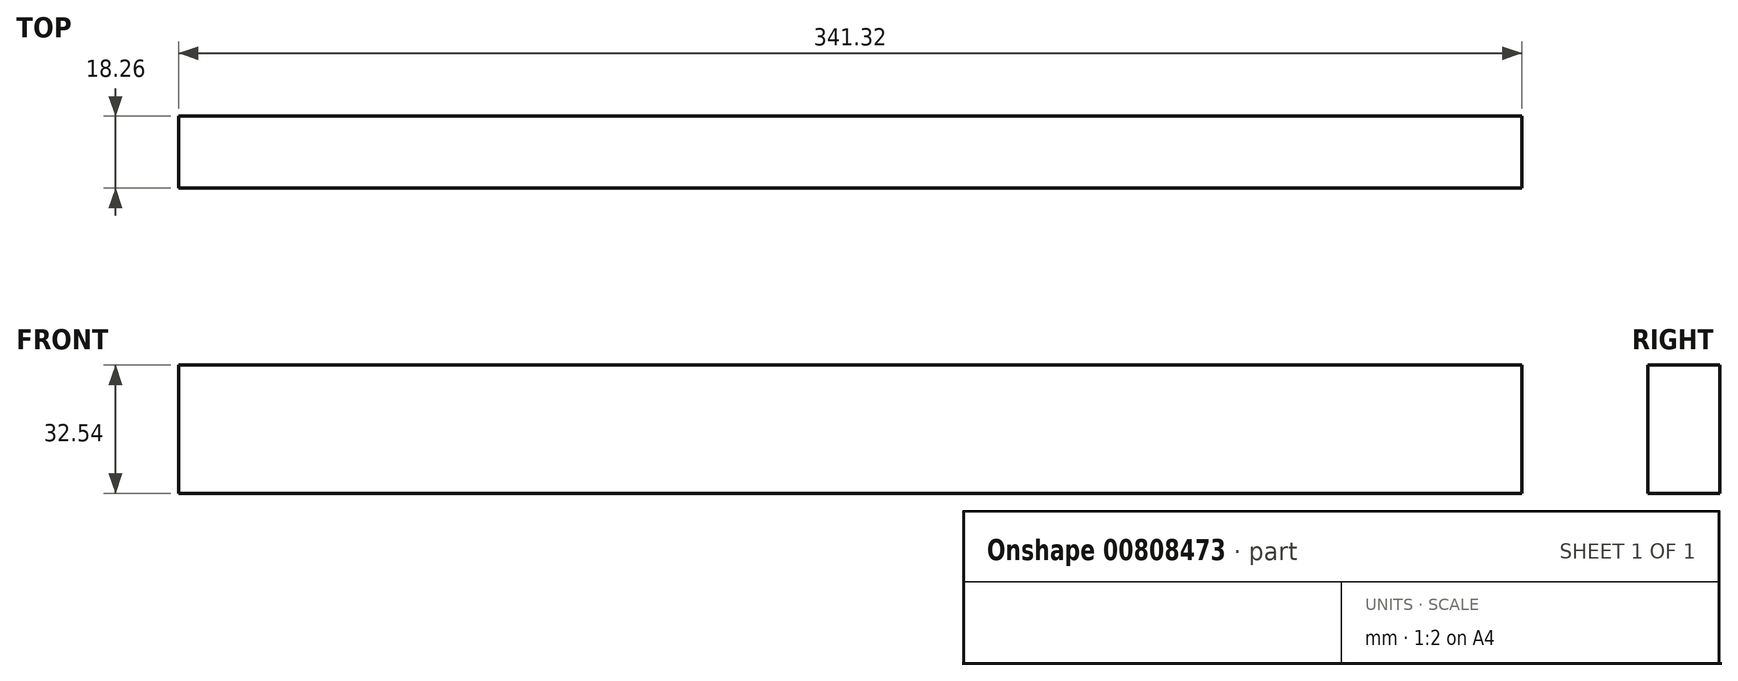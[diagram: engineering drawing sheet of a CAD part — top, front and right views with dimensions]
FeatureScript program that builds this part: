
annotation { "Feature Type Name" : "Feature", "Feature Type Description" : "" }
export const myFeature = defineFeature(function(context is Context, id is Id, definition is map)
    precondition{}
    {
        {
            var Q0;
            Q0=qCreatedBy(makeId("Front.planeOp"),FACE);
            var sketch = newSketch(context, id + "F0", { "sketchPlane" : qUnion([Q0])});
            skLineSegment(sketch, "E0.bottom", {"start": v(170.66, 16.27) * mm, "end": v(-170.66, 16.27) * mm});
            skLineSegment(sketch, "E0.top", {"start": v(170.66, -16.27) * mm, "end": v(-170.66, -16.27) * mm});
            skLineSegment(sketch, "E0.left", {"start": v(170.66, 16.27) * mm, "end": v(170.66, -16.27) * mm});
            skLineSegment(sketch, "E0.right", {"start": v(-170.66, 16.27) * mm, "end": v(-170.66, -16.27) * mm});
            skPoint(sketch, "E0.middle", {"position": v(0, 0) * mm});
            skSolve(sketch);
        }
        {
            var Q0;
            Q0 = qSketchRegion(id + "F0", true);
            extrude(context, id + "F1", {"entities" : qUnion([Q0]), "depth" : 18.26 * mm, "offsetDistance" : 25.4 * mm});
        }
    });
